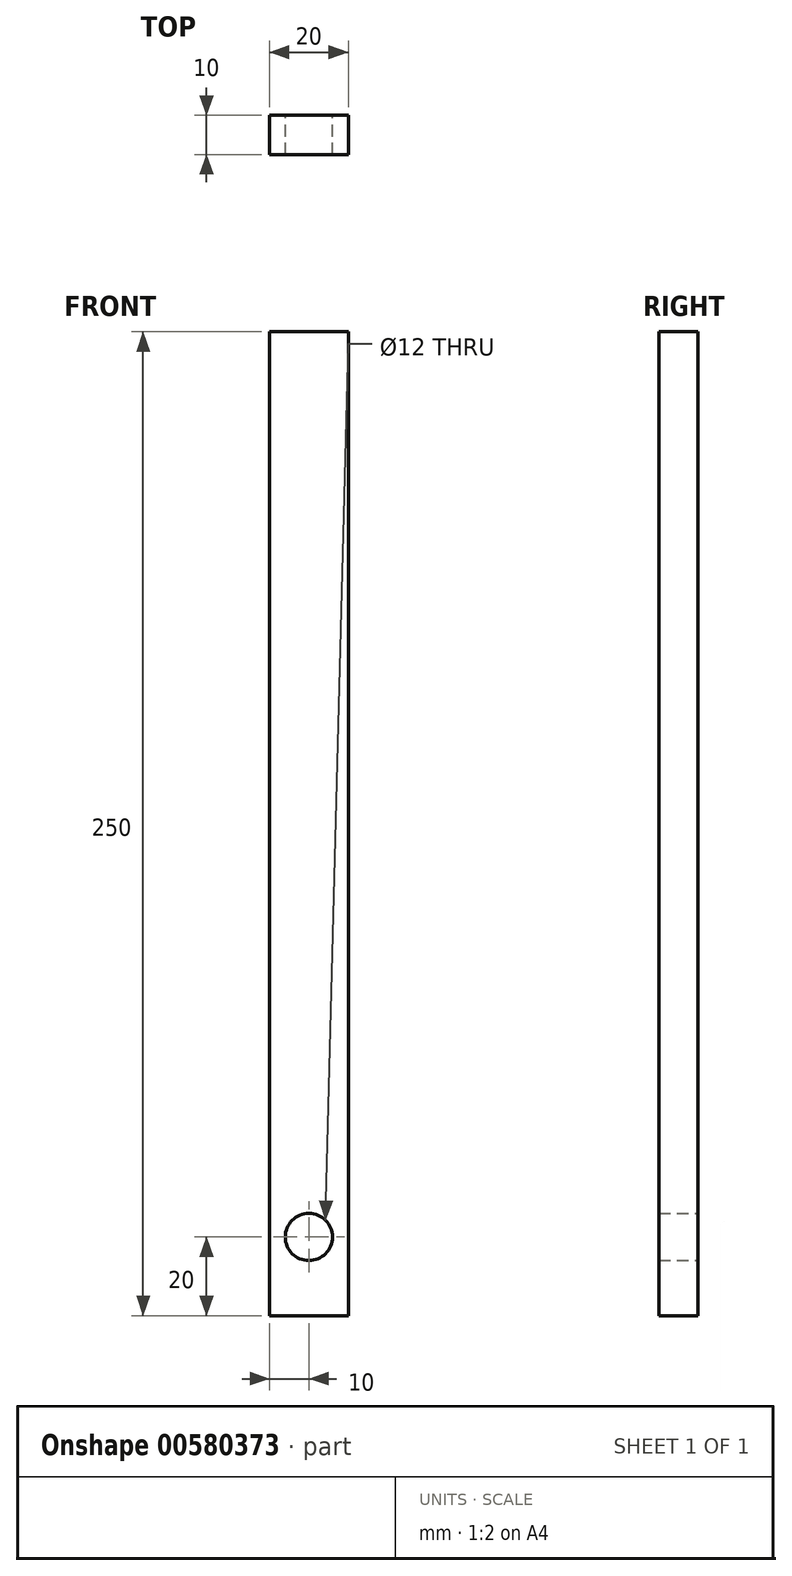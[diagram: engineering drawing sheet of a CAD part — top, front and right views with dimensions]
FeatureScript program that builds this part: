
annotation { "Feature Type Name" : "Feature", "Feature Type Description" : "" }
export const myFeature = defineFeature(function(context is Context, id is Id, definition is map)
    precondition{}
    {
        {
            var Q0;
            Q0=qCreatedBy(makeId("Front.planeOp"),FACE);
            var sketch = newSketch(context, id + "F0", { "sketchPlane" : qUnion([Q0])});
            skLineSegment(sketch, "E0.bottom", {"start": v(0, 0) * mm, "end": v(20, 0) * mm});
            skLineSegment(sketch, "E0.top", {"start": v(0, 250) * mm, "end": v(20, 250) * mm});
            skLineSegment(sketch, "E0.left", {"start": v(0, 0) * mm, "end": v(0, 250) * mm});
            skLineSegment(sketch, "E0.right", {"start": v(20, 0) * mm, "end": v(20, 250) * mm});
            skCircle(sketch, "E1", {"center": v(10, 20) * mm, "radius": 6 * mm});
            skPoint(sketch, "E1.centerSnap0", {"position": v(10, 0) * mm});
            skSolve(sketch);
        }
        {
            var Q0;
            Q0=makeQuery(id+"F0.imprint","IMPRINT",FACE,{"disambiguationData":[TD([[makeQuery(id+"F0.imprint","IMPRINT",EDGE,{"derivedFrom":sQuery(id+"F0.wireOp",EDGE,"E0.bottom")}),1.0]])]});
            extrude(context, id + "F1", {"entities" : qUnion([Q0]), "depth" : 10 * mm, "offsetDistance" : 25 * mm});
        }
    });
